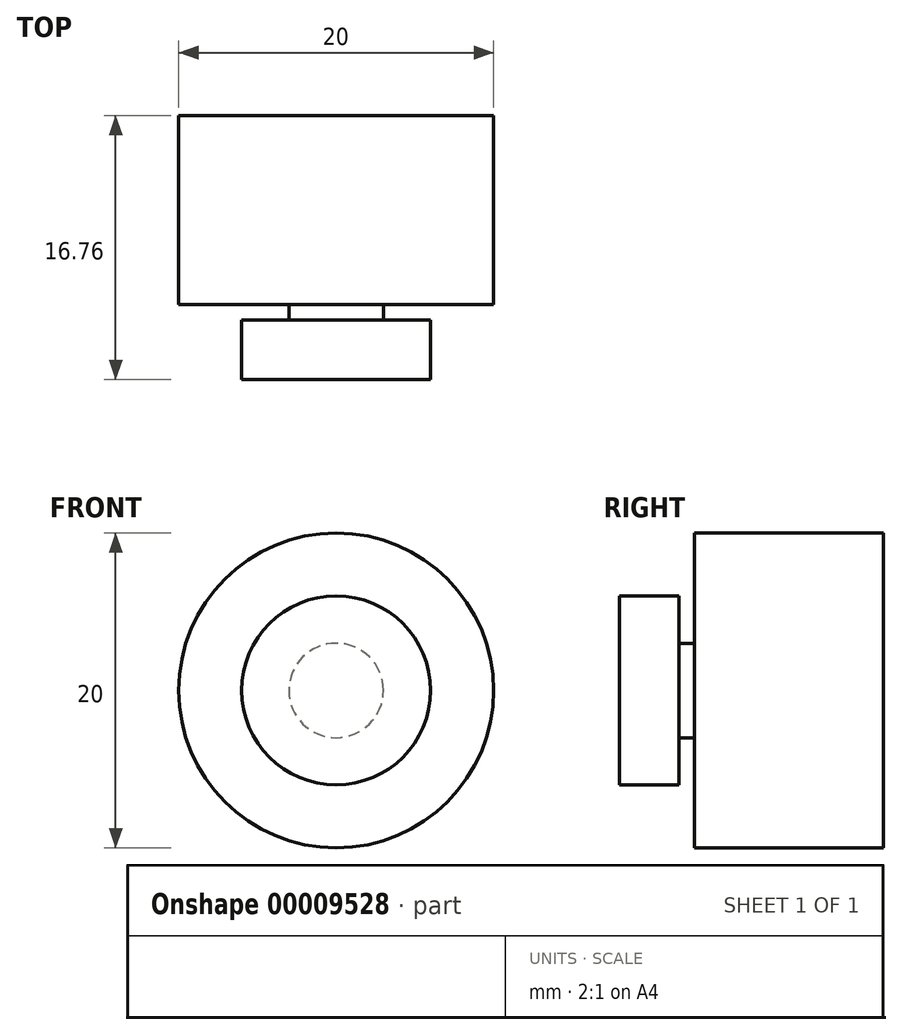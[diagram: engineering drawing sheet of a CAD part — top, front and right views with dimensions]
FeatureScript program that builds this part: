
annotation { "Feature Type Name" : "Feature", "Feature Type Description" : "" }
export const myFeature = defineFeature(function(context is Context, id is Id, definition is map)
    precondition{}
    {
        {
            var Q0;
            Q0=qCreatedBy(makeId("Right.planeOp"),FACE);
            var sketch = newSketch(context, id + "F0", { "sketchPlane" : qUnion([Q0])});
            skLineSegment(sketch, "E0.bottom", {"start": v(0, 0) * mm, "end": v(3.76, 0) * mm});
            skLineSegment(sketch, "E0.top", {"start": v(0, 6) * mm, "end": v(3.76, 6) * mm});
            skLineSegment(sketch, "E0.left", {"start": v(0, 0) * mm, "end": v(0, 6) * mm});
            skLineSegment(sketch, "E0.right", {"start": v(3.76, 0) * mm, "end": v(3.76, 6) * mm});
            skLineSegment(sketch, "E1.bottom", {"start": v(3.76, 0) * mm, "end": v(4.76, 0) * mm});
            skLineSegment(sketch, "E1.top", {"start": v(3.76, 3) * mm, "end": v(4.76, 3) * mm});
            skLineSegment(sketch, "E1.left", {"start": v(3.76, 0) * mm, "end": v(3.76, 3) * mm});
            skLineSegment(sketch, "E1.right", {"start": v(4.76, 0) * mm, "end": v(4.76, 3) * mm});
            skLineSegment(sketch, "E2.bottom", {"start": v(4.76, 0) * mm, "end": v(16.76, 0) * mm});
            skLineSegment(sketch, "E2.top", {"start": v(4.76, 10) * mm, "end": v(16.76, 10) * mm});
            skLineSegment(sketch, "E2.left", {"start": v(4.76, 0) * mm, "end": v(4.76, 10) * mm});
            skLineSegment(sketch, "E2.right", {"start": v(16.76, 0) * mm, "end": v(16.76, 10) * mm});
            skSolve(sketch);
        }
        {
            var Q0;
            Q0=makeQuery(id+"F0.imprint","IMPRINT",FACE,{"disambiguationData":[TD([[makeQuery(id+"F0.imprint","IMPRINT",EDGE,{"derivedFrom":sQuery(id+"F0.wireOp",EDGE,"E0.bottom")}),1.0]])]});
            var Q1;
            {var subQ2=sQuery(id+"F0.wireOp",EDGE,"E1.bottom");Q1=makeQuery(id+"F0.imprint","IMPRINT",FACE,{"disambiguationData":[TD([[makeQuery(id+"F0.imprint","IMPRINT",EDGE,{"derivedFrom":subQ2}),1.0]])]});}
            var Q2;
            {var subQ3=sQuery(id+"F0.wireOp",EDGE,"E2.bottom");Q2=makeQuery(id+"F0.imprint","IMPRINT",FACE,{"disambiguationData":[TD([[makeQuery(id+"F0.imprint","IMPRINT",EDGE,{"derivedFrom":subQ3}),1.0]])]});}
            var Q3;
            Q3=sQuery(id+"F0.wireOp",EDGE,"E2.bottom");
            revolve(context, id + "F1", {"entities" : qUnion([Q0, Q1, Q2]), "axis" : qUnion([Q3]), "revolveType" : RevolveType.FULL});
        }
    });
